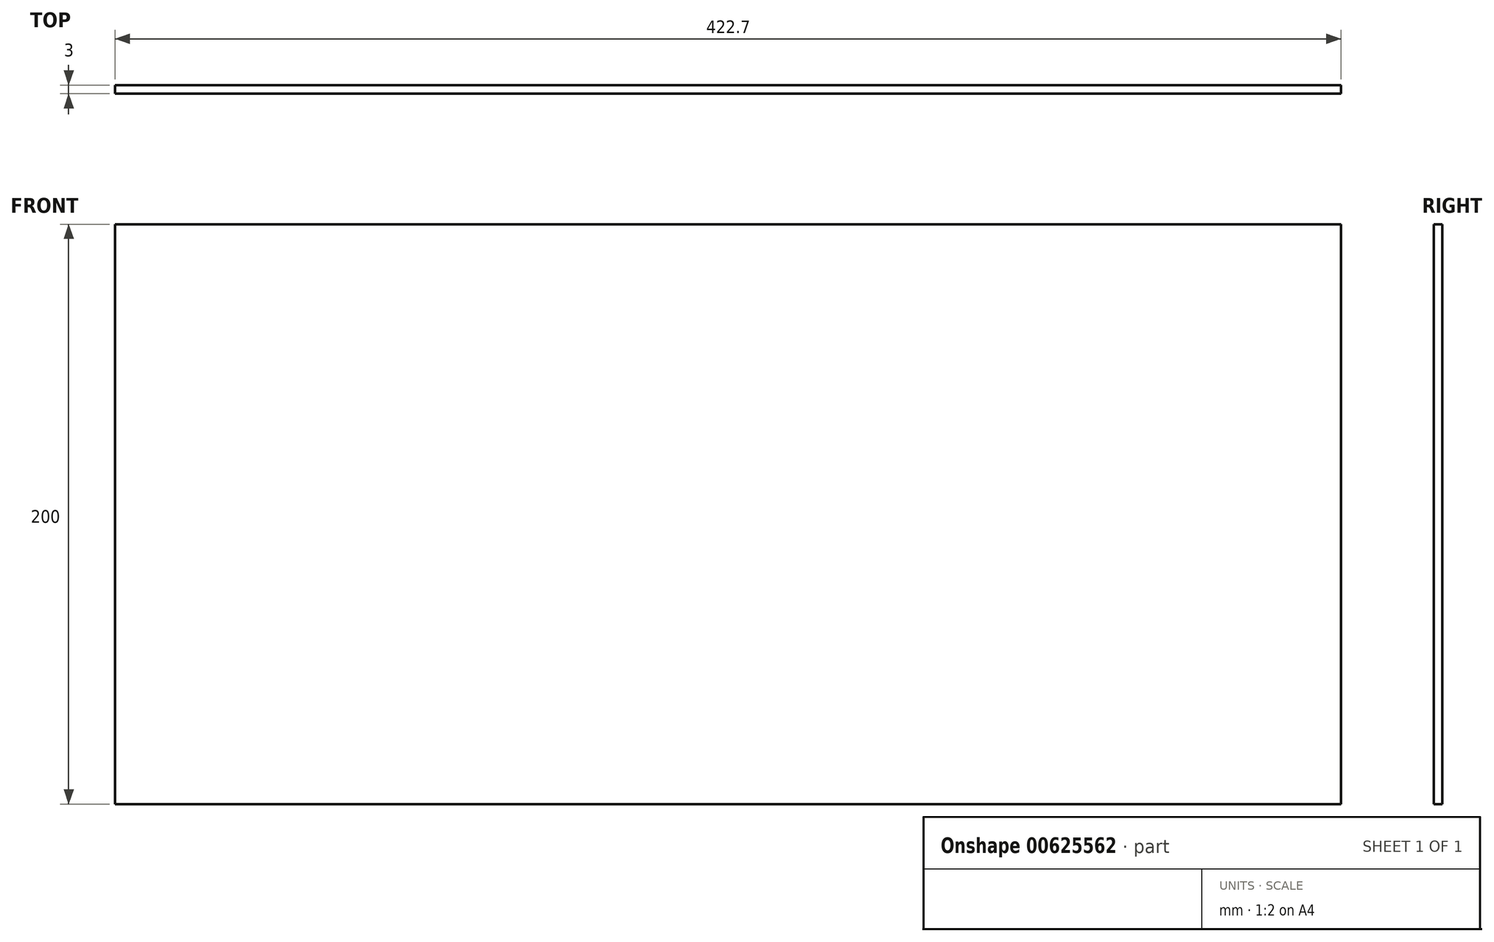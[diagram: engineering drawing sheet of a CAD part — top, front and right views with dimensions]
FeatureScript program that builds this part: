
annotation { "Feature Type Name" : "Feature", "Feature Type Description" : "" }
export const myFeature = defineFeature(function(context is Context, id is Id, definition is map)
    precondition{}
    {
        {
            var Q0;
            Q0=qCreatedBy(makeId("Front.planeOp"),FACE);
            var sketch = newSketch(context, id + "F0", { "sketchPlane" : qUnion([Q0])});
            skLineSegment(sketch, "E0.bottom", {"start": v(-211.35, 100) * mm, "end": v(211.35, 100) * mm});
            skLineSegment(sketch, "E0.top", {"start": v(-211.35, -100) * mm, "end": v(211.35, -100) * mm});
            skLineSegment(sketch, "E0.left", {"start": v(-211.35, 100) * mm, "end": v(-211.35, -100) * mm});
            skLineSegment(sketch, "E0.right", {"start": v(211.35, 100) * mm, "end": v(211.35, -100) * mm});
            skPoint(sketch, "E0.middle", {"position": v(0, 0) * mm});
            skSolve(sketch);
        }
        {
            var Q0;
            Q0 = qSketchRegion(id + "F0", true);
            extrude(context, id + "F1", {"entities" : qUnion([Q0]), "depth" : 3 * mm, "offsetDistance" : 25 * mm});
        }
    });
